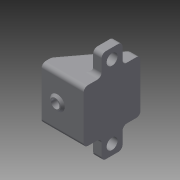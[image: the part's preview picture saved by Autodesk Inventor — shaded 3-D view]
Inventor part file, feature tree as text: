
AUTODESK INVENTOR PART (.ipt)
format: ipt  version: 2015 (Build 190159000, 159)  size: 166,912 bytes
history: native  units: in
note: dims shown in document units (in); Inventor stores cm internally (conversion verified against a paired STEP export)
features: sketch x8, other x3, plane x2
ambient origin geometry x8: Origin, YZ Plane, XZ Plane, XY Plane, X Axis, Y Axis, Z Axis, Center Point
bodies: Solid1 (feature_tree)
feature tree (13):
  other  "holder1.ipt"
  other  "Solid1::holder1.ipt"
  other  "TaggingFeature1"
  sketch  "Sketch1"  dims[d0=0.3937in]
  sketch  "Sketch2"
  sketch  "Sketch3"
  sketch  "Sketch4"
  sketch  "Sketch5"
  sketch  "Sketch6"
  sketch  "Sketch7"
  sketch  "Sketch8"
  plane  "Work Plane1"
  plane  "Work Plane2"
